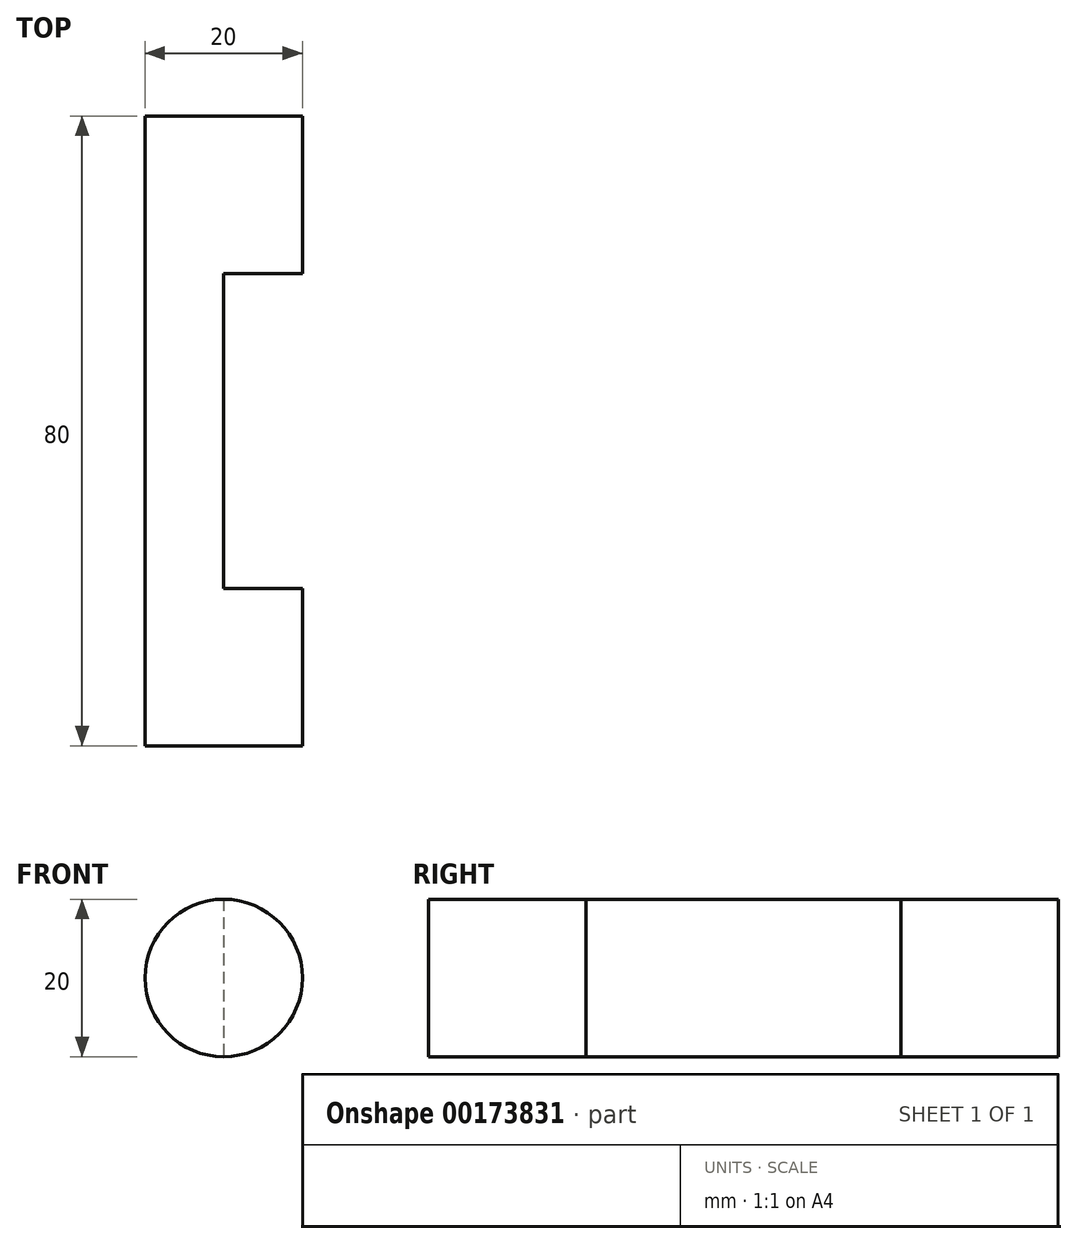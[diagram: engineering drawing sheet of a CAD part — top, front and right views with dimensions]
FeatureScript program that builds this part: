
annotation { "Feature Type Name" : "Feature", "Feature Type Description" : "" }
export const myFeature = defineFeature(function(context is Context, id is Id, definition is map)
    precondition{}
    {
        {
            var Q0;
            Q0=qCreatedBy(makeId("Front.planeOp"),FACE);
            var sketch = newSketch(context, id + "F0", { "sketchPlane" : qUnion([Q0])});
            skCircle(sketch, "E0", {"center": v(0, 0) * mm, "radius": 10 * mm});
            skSolve(sketch);
        }
        {
            var Q0;
            Q0 = qSketchRegion(id + "F0", true);
            extrude(context, id + "F1", {"entities" : qUnion([Q0]), "depth" : 80 * mm});
        }
        {
            var Q0;
            Q0=qCreatedBy(makeId("Right.planeOp"),FACE);
            cPlane(context, id + "F2", {"entities" : qUnion([Q0]), "cplaneType" : CPlaneType.OFFSET, "offset" : 10 * mm, "width" : 150 * mm, "height" : 150 * mm});
        }
        {
            var Q0;
            Q0=qCreatedBy(id+"F2.planeOp",FACE);
            var sketch = newSketch(context, id + "F3", { "sketchPlane" : qUnion([Q0])});
            skLineSegment(sketch, "E1.bottom", {"start": v(-60, 10) * mm, "end": v(-20, 10) * mm});
            skLineSegment(sketch, "E1.top", {"start": v(-60, -10) * mm, "end": v(-20, -10) * mm});
            skLineSegment(sketch, "E1.left", {"start": v(-60, 10) * mm, "end": v(-60, -10) * mm});
            skLineSegment(sketch, "E1.right", {"start": v(-20, 10) * mm, "end": v(-20, -10) * mm});
            skSolve(sketch);
        }
        {
            var Q0;
            Q0 = qSketchRegion(id + "F3", true);
            extrude(context, id + "F4", {"entities" : qUnion([Q0]), "operationType" : NewBodyOperationType.REMOVE, "oppositeDirection" : true, "depth" : 10 * mm});
        }
    });
